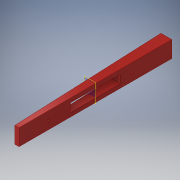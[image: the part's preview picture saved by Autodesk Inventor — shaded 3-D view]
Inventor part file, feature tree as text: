
AUTODESK INVENTOR PART (.ipt)
format: ipt  version: 2019.1 (Build 231200000, 200)  size: 158,208 bytes
history: native  units: in
note: dims shown in document units (in); Inventor stores cm internally (conversion verified against a paired STEP export)
features: sketch x5, extrude x4, plane x2, hole x1
ambient origin geometry x8: Origin, YZ Plane, XZ Plane, XY Plane, X Axis, Y Axis, Z Axis, Center Point
bodies: Solid1 (feature_tree)
feature tree (12):
  extrude  "Extrusion1"  Depth=18.5in
  plane  "Work Plane1"
  extrude  "Extrusion2"  TaperAngle=0.0deg  [1 undecoded]
  hole  "Hole2"  [1 undecoded]
  extrude  "Extrusion3"  Depth=1.0in
  plane  "Work Plane2"
  extrude  "Extrusion4"  Depth=0.4375in
  sketch  "Sketch1"  dims[d0=18.5in d1=0.0172in]
  sketch  "Sketch2"  dims[d2=2.0in d3=0.0in]
  sketch  "Sketch4"  dims[d4=0.5in d5=0.0in]
  sketch  "Sketch6"  dims[d16=1.0in d17=3.5in]
  sketch  "Sketch8"  dims[d18=13.625in d19=0.266in d20=0.75in d21=0.7in d22=1.65in d23=0.5635in d24=1.0in d25=0.8108in d26=0.4375in d27=0.92in d28=0.0in d29=-9.25in d30=1.0in d31=6.0in d32=1.0in d33=0.0in]
note: 2 required parameter values undecoded (feature->parameter linkage not recoverable at this tier; creation-order binding heuristic only, values carry confidence <= 0.55)
